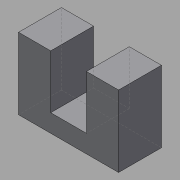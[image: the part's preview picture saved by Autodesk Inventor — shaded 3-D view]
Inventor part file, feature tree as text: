
AUTODESK INVENTOR PART (.ipt)
format: ipt  version: 2015 (Build 190159000, 159)  size: 77,312 bytes
history: native  units: in
note: dims shown in document units (in); Inventor stores cm internally (conversion verified against a paired STEP export)
features: other x3, sketch x2
ambient origin geometry x8: Origin, YZ Plane, XZ Plane, XY Plane, X Axis, Y Axis, Z Axis, Center Point
bodies: Solid1 (feature_tree)
feature tree (5):
  other  "opto_MIR3.ipt"
  other  "Solid1::opto_MIR3.ipt"
  other  "TaggingFeature1"
  sketch  "Sketch1"  dims[d0=0.3937in]
  sketch  "Sketch2"
